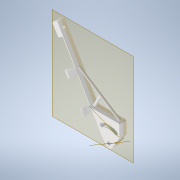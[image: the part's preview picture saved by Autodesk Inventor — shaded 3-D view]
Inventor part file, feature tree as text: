
AUTODESK INVENTOR PART (.ipt)
format: ipt  version: 2020 (Build 240168000, 168)  size: 282,112 bytes
history: native  units: mm
features: sketch x15, extrude x9, other x5, plane x3, reference x3, sweep x2, fillet x2, chamfer x1
ambient origin geometry x8: Origin, YZ Plane, XZ Plane, XY Plane, X Axis, Y Axis, Z Axis, Center Point
bodies: Volumenkörper1 (feature_tree)
feature tree (40):
  extrude  "Extrusion1"  Depth=4.0mm
  extrude  "Extrusion2"  Depth=4.0mm
  extrude  "Extrusion3"  Depth=6.0mm
  other  "Arbeitsachse1"
  other  "Arbeitspunkt1"
  plane  "Arbeitsebene1"
  sketch  "Skizze4"  dims[d9=1.5mm d10=10.0mm d11=0.0mm d12=0.0mm d13=0.0mm]
  sketch  "Skizze5"  dims[d14=3.0mm d15=0.0mm]
  extrude  "Extrusion4"  Depth=10.0mm TaperAngle=0.0deg
  chamfer  "Fase1"  [1 undecoded]
  plane  "Arbeitsebene2"
  sweep  "Sweeping2"
  sketch  "Skizze9"  dims[d25=2.0mm d28=0.0mm d29=0.0mm]
  plane  "Arbeitsebene3"
  sweep  "Sweeping3"
  fillet  "Rundung1"  Radius=3.0mm
  extrude  "Extrusion5"  Depth=3.0mm
  extrude  "Extrusion6"  TaperAngle=0.0deg  [1 undecoded]
  extrude  "Extrusion7"  TaperAngle=0.0deg  [1 undecoded]
  extrude  "Extrusion8"  Depth=10.0mm
  extrude  "Extrusion9"  Depth=5.0mm
  fillet  "Rundung2"  Radius=0.914mm
  sketch  "Skizze1"  dims[d1=4.0mm d2=15.0mm]
  reference  "Referenz1"
  reference  "Referenz2"
  sketch  "Skizze2"  dims[d3=15.0mm d5=4.0mm]
  sketch  "Skizze3"  dims[d6=6.0mm d7=0.0mm d8=27.003mm]
  reference  "Referenz3"
  sketch  "Skizze6"  dims[d16=5.0mm d17=80.0mm d18=0.0mm]
  sketch  "Skizze7"  dims[d19=2.0mm d20=2.0mm d21=45.0deg d22=3.0mm]
  sketch  "Skizze8"  dims[d23=40.0mm d24=3.0mm]
  sketch  "Skizze10"  dims[d30=2.0mm d31=0.0mm d32=0.0mm]
  sketch  "Skizze11"  dims[d33=1.0mm d34=10.0mm]
  sketch  "Skizze12"  dims[d35=5.0mm d36=0.0mm d37=2.1mm d38=0.914mm d39=0.0mm]
  sketch  "Skizze13"  dims[d40=5.0mm]
  sketch  "Skizze14"  dims[d41=5.0mm]
  sketch  "Skizze15"  dims[d42=20.0mm d43=20.0mm d44=6.0mm d45=0.0mm d46=4.0mm d47=4.0mm d48=6.0mm d49=0.0mm d50=4.0mm d51=4.0mm d52=6.0mm d53=0.0mm d54=1.0mm]
  parser-record x1  (decoder bookkeeping rows leaked as tree rows — omitted from the tree; the rows remain in map.json)
  other  "GlassesAssembly.iam"
  other  "CemaraArmInterface:1"
note: 3 required parameter values undecoded (feature->parameter linkage not recoverable at this tier; creation-order binding heuristic only, values carry confidence <= 0.55)
note: 1 file-system path scrubbed to <path> (originals preserved in map.json)
